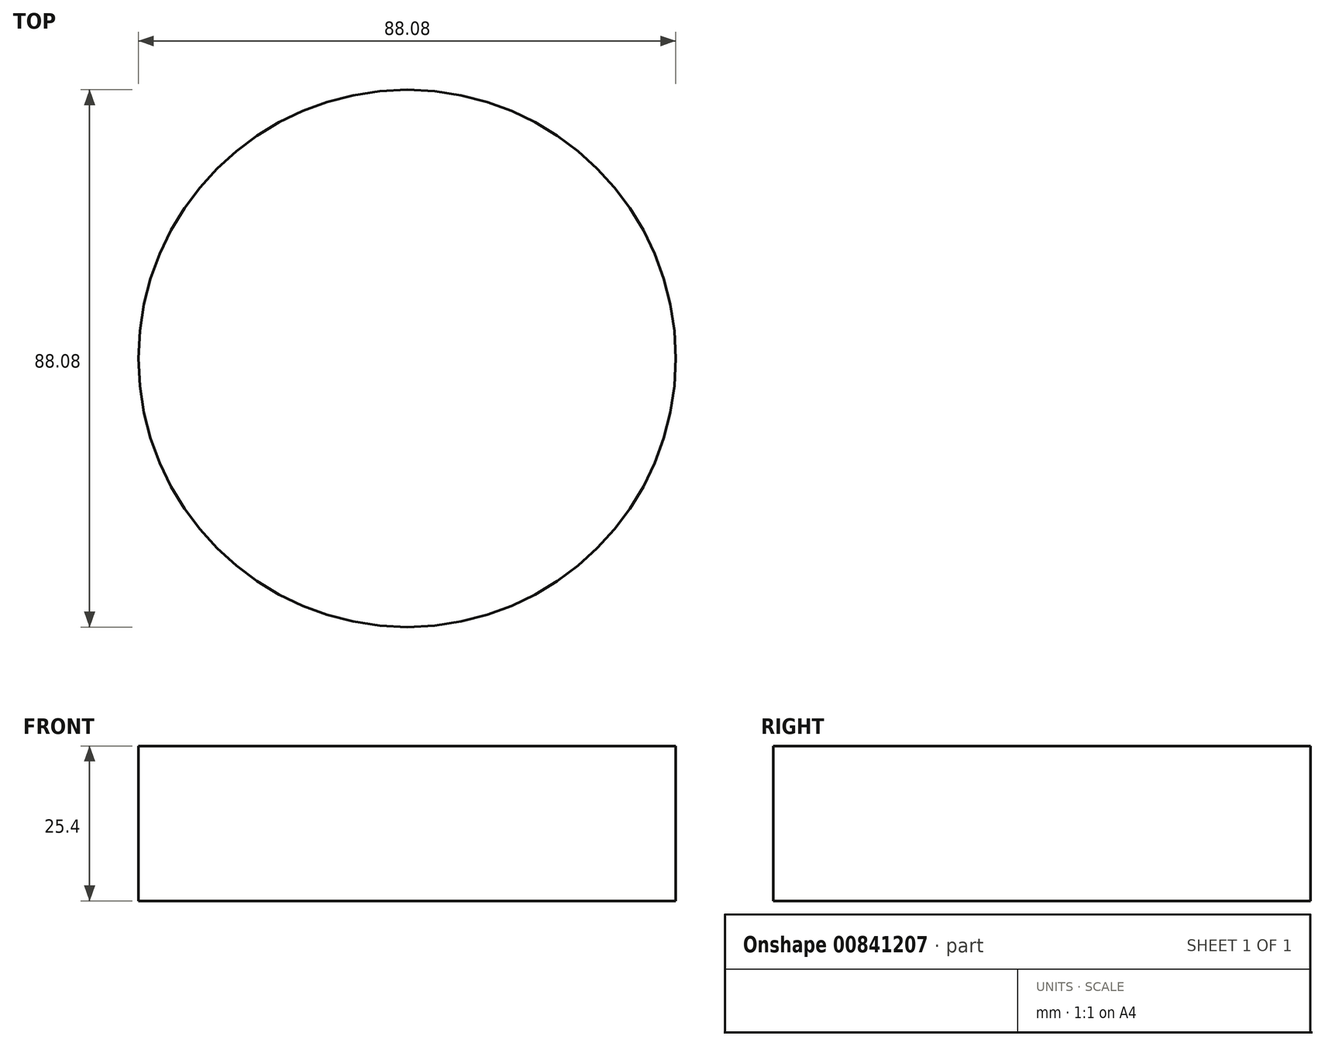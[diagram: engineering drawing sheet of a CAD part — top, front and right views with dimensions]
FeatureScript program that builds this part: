
annotation { "Feature Type Name" : "Feature", "Feature Type Description" : "" }
export const myFeature = defineFeature(function(context is Context, id is Id, definition is map)
    precondition{}
    {
        {
            var Q0;
            Q0=qCreatedBy(makeId("Top.planeOp"),FACE);
            var sketch = newSketch(context, id + "F0", { "sketchPlane" : qUnion([Q0])});
            skCircle(sketch, "E0", {"center": v(-25.26, 27.03) * mm, "radius": 44.04 * mm});
            skSolve(sketch);
        }
        {
            var Q0;
            Q0=makeQuery(id+"F0.imprint","IMPRINT",FACE,{"disambiguationData":[TD([[makeQuery(id+"F0.imprint","IMPRINT",EDGE,{"derivedFrom":sQuery(id+"F0.wireOp",EDGE,"E0")}),1.0]])]});
            extrude(context, id + "F1", {"entities" : qUnion([Q0]), "depth" : 25.4 * mm, "offsetDistance" : 25.4 * mm});
        }
    });
